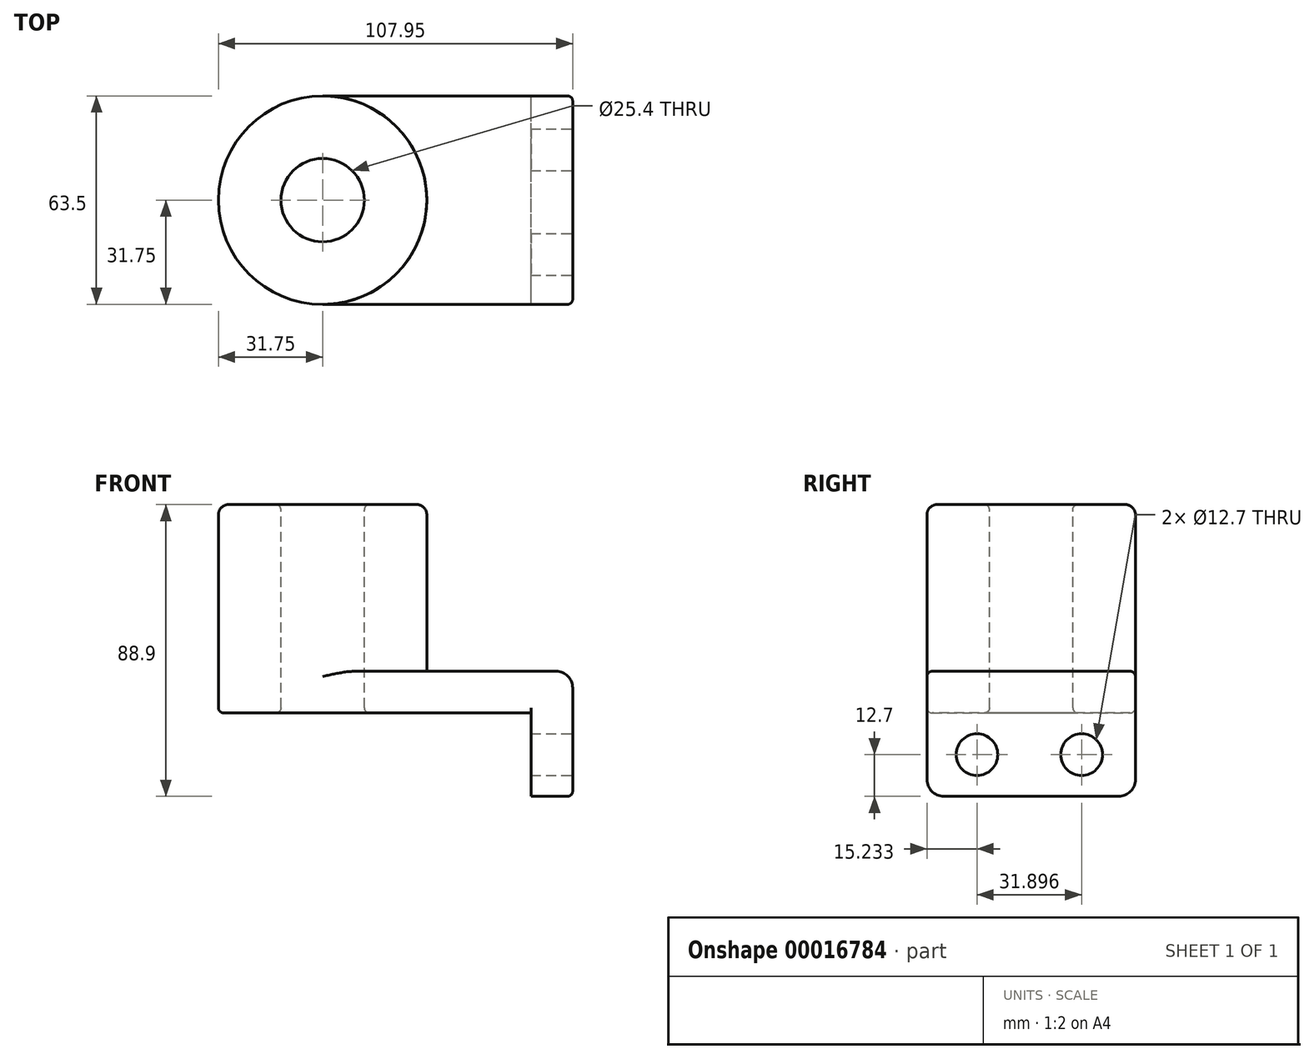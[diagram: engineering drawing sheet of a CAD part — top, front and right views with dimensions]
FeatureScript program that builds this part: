
annotation { "Feature Type Name" : "Feature", "Feature Type Description" : "" }
export const myFeature = defineFeature(function(context is Context, id is Id, definition is map)
    precondition{}
    {
        {
            var Q0;
            Q0=qCreatedBy(makeId("Top.planeOp"),FACE);
            var sketch = newSketch(context, id + "F0", { "sketchPlane" : qUnion([Q0])});
            skLineSegment(sketch, "E0.rect.bottom", {"start": v(38.1, -31.75) * mm, "end": v(-38.1, -31.75) * mm});
            skLineSegment(sketch, "E0.rect.top", {"start": v(38.1, 31.75) * mm, "end": v(-38.1, 31.75) * mm});
            skLineSegment(sketch, "E0.rect.left", {"start": v(38.1, -31.75) * mm, "end": v(38.1, 31.75) * mm});
            skLineSegment(sketch, "E0.rect.right", {"start": v(-38.1, -31.75) * mm, "end": v(-38.1, 31.75) * mm});
            skPoint(sketch, "E0.rect.middle", {"position": v(0, 0) * mm});
            skCircle(sketch, "E1", {"center": v(-38.1, 0) * mm, "radius": 31.75 * mm});
            skCircle(sketch, "E2", {"center": v(-38.1, 0) * mm, "radius": 12.7 * mm});
            skSolve(sketch);
        }
        {
            var Q0;
            Q0 = qSketchRegion(id + "F0", true);
            extrude(context, id + "F1", {"entities" : qUnion([Q0]), "oppositeDirection" : true, "depth" : 12.7 * mm});
        }
        {
            var Q0;
            {var subQ0=sQuery(id+"F0.wireOp",EDGE,"E2");var subQ1=sQuery(id+"F0.wireOp",EDGE,"E0.rect.right");var subQ3=makeQuery(id+"F0.imprint","INTERSECT",VERTEX,{"disambiguationData":[OD(0.0)],"derivedFrom":[subQ1,subQ0]});Q0=makeQuery(id+"F0.imprint","IMPRINT",FACE,{"disambiguationData":[TD([[makeQuery(id+"F0.imprint","IMPRINT",EDGE,{"disambiguationData":[TD([[subQ3,1.0]])],"derivedFrom":subQ0}),-1.0]])]});}
            var Q1;
            {var subQ0=sQuery(id+"F0.wireOp",EDGE,"E2");var subQ1=sQuery(id+"F0.wireOp",EDGE,"E0.rect.right");var subQ3=makeQuery(id+"F0.imprint","INTERSECT",VERTEX,{"disambiguationData":[OD(0.0)],"derivedFrom":[subQ1,subQ0]});Q1=makeQuery(id+"F0.imprint","IMPRINT",FACE,{"disambiguationData":[TD([[makeQuery(id+"F0.imprint","IMPRINT",EDGE,{"disambiguationData":[TD([[subQ3,-1.0]])],"derivedFrom":subQ0}),-1.0]])]});}
            extrude(context, id + "F2", {"entities" : qUnion([Q0, Q1]), "operationType" : NewBodyOperationType.ADD, "depth" : 50.8 * mm});
        }
        {
            var Q0;
            Q0=makeQuery(id+"F1.opExtrude","SWEPT_FACE",FACE,{"disambiguationData":[OSD([sQuery(id+"F0.wireOp",EDGE,"E0.rect.left")])]});
            var sketch = newSketch(context, id + "F3", { "sketchPlane" : qUnion([Q0])});
            skLineSegment(sketch, "E3.bottom", {"start": v(-31.75, 0) * mm, "end": v(31.75, 0) * mm});
            skLineSegment(sketch, "E3.top", {"start": v(-31.75, -38.1) * mm, "end": v(31.75, -38.1) * mm});
            skLineSegment(sketch, "E3.left", {"start": v(-31.75, 0) * mm, "end": v(-31.75, -38.1) * mm});
            skLineSegment(sketch, "E3.right", {"start": v(31.75, 0) * mm, "end": v(31.75, -38.1) * mm});
            skCircle(sketch, "E4", {"center": v(-16.52, -25.4) * mm, "radius": 6.35 * mm});
            skCircle(sketch, "E5", {"center": v(15.38, -25.4) * mm, "radius": 6.35 * mm});
            skLineSegment(sketch, "E6", {"start": v(0, -12.7) * mm, "end": v(0, -38.1) * mm, "construction": true});
            skSolve(sketch);
        }
        {
            var Q0;
            {var subQ2=sQuery(id+"F3.wireOp",EDGE,"E3.top");Q0=makeQuery(id+"F3.imprint","IMPRINT",FACE,{"disambiguationData":[TD([[makeQuery(id+"F3.imprint","IMPRINT",EDGE,{"derivedFrom":subQ2}),1.0]])]});}
            extrude(context, id + "F4", {"entities" : qUnion([Q0]), "operationType" : NewBodyOperationType.ADD, "oppositeDirection" : true, "depth" : 12.7 * mm});
        }
        {
            var Q0;
            Q0=makeQuery(id+"F2.opExtrude","CAP_EDGE",EDGE,{"disambiguationData":[OSD([sQuery(id+"F0.wireOp",EDGE,"E1")])],"isStart":true});
            var Q1;
            Q1=makeQuery(id+"F1.opExtrude","CAP_EDGE",EDGE,{"disambiguationData":[OSD([sQuery(id+"F0.wireOp",EDGE,"E0.rect.left")])],"isStart":true});
            var Q2;
            Q2=makeQuery(id+"F4.opExtrude","SWEPT_EDGE",EDGE,{"disambiguationData":[OSD([sQuery(id+"F3.wireOp",EDGE,"E3.top"),sQuery(id+"F3.wireOp",EDGE,"E3.left")])]});
            var Q3;
            Q3=makeQuery(id+"F4.opExtrude","SWEPT_EDGE",EDGE,{"disambiguationData":[OSD([sQuery(id+"F3.wireOp",EDGE,"E3.top"),sQuery(id+"F3.wireOp",EDGE,"E3.right")])]});
            fillet(context, id + "F5", {"entities" : qUnion([Q0, Q1, Q2, Q3]), "radius" : 5.08 * mm, "tangentPropagation" : true, "allowEdgeOverflow" : false});
        }
        {
            var Q0;
            Q0=makeQuery(id+"F1.opExtrude","CAP_EDGE",EDGE,{"disambiguationData":[OSD([sQuery(id+"F0.wireOp",EDGE,"E0.rect.bottom")])],"isStart":true});
            var Q1;
            Q1=makeQuery(id+"F1.opExtrude","CAP_EDGE",EDGE,{"disambiguationData":[OSD([sQuery(id+"F0.wireOp",EDGE,"E0.rect.top")])],"isStart":true});
            var Q2;
            Q2=makeQuery(id+"F4.boolean.opBoolean","MERGE",EDGE,{"derivedFrom":[makeQuery(id+"F1.opExtrude","SWEPT_EDGE",EDGE,{"disambiguationData":[OSD([sQuery(id+"F0.wireOp",EDGE,"E0.rect.top"),sQuery(id+"F0.wireOp",EDGE,"E0.rect.left")])]}),makeQuery(id+"F4.opExtrude","CAP_EDGE",EDGE,{"disambiguationData":[OSD([sQuery(id+"F3.wireOp",EDGE,"E3.right")])],"isStart":true})]});
            var Q3;
            Q3=makeQuery(id+"F1.opExtrude","CAP_EDGE",EDGE,{"disambiguationData":[OSD([sQuery(id+"F0.wireOp",EDGE,"E0.rect.bottom")])],"isStart":false});
            var Q4;
            Q4=makeQuery(id+"F4.opExtrude","CAP_EDGE",EDGE,{"disambiguationData":[OSD([sQuery(id+"F0.wireOp",EDGE,"E0.rect.left")])],"isStart":false});
            var Q5;
            {var subQ0=sQuery(id+"F0.wireOp",EDGE,"E2");Q5=makeQuery(id+"F2.boolean.opBoolean","MERGE",FACE,{"derivedFrom":[makeQuery(id+"F1.opExtrude","SWEPT_FACE",FACE,{"disambiguationData":[OSD([subQ0])]}),makeQuery(id+"F2.opExtrude","SWEPT_FACE",FACE,{"disambiguationData":[OSD([subQ0])]})]});}
            fillet(context, id + "F6", {"entities" : qUnion([Q0, Q1, Q2, Q3, Q4, Q5]), "radius" : 1.59 * mm, "tangentPropagation" : true, "allowEdgeOverflow" : false});
        }
        {
            var Q0;
            Q0=makeQuery(id+"F2.opExtrude","CAP_EDGE",EDGE,{"disambiguationData":[OSD([sQuery(id+"F0.wireOp",EDGE,"E1")])],"isStart":false});
            fillet(context, id + "F7", {"entities" : qUnion([Q0]), "radius" : 3.05 * mm, "tangentPropagation" : true, "allowEdgeOverflow" : false});
        }
    });
